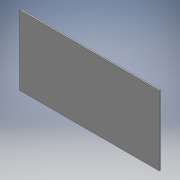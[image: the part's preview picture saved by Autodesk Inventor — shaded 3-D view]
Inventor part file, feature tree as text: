
AUTODESK INVENTOR PART (.ipt)
format: ipt  version: 2016 (Build 200138000, 138)  size: 86,016 bytes
history: native  units: mm
features: extrude x1, sketch x1
ambient origin geometry x8: Origin, YZ Plane, XZ Plane, XY Plane, X Axis, Y Axis, Z Axis, Center Point
bodies: Solid1 (feature_tree)
feature tree (2):
  extrude  "Extrusion1"  Depth=800.0mm
  sketch  "Sketch1"  dims[d0=400.0mm d1=800.0mm d2=6.0mm d3=0.0mm]
